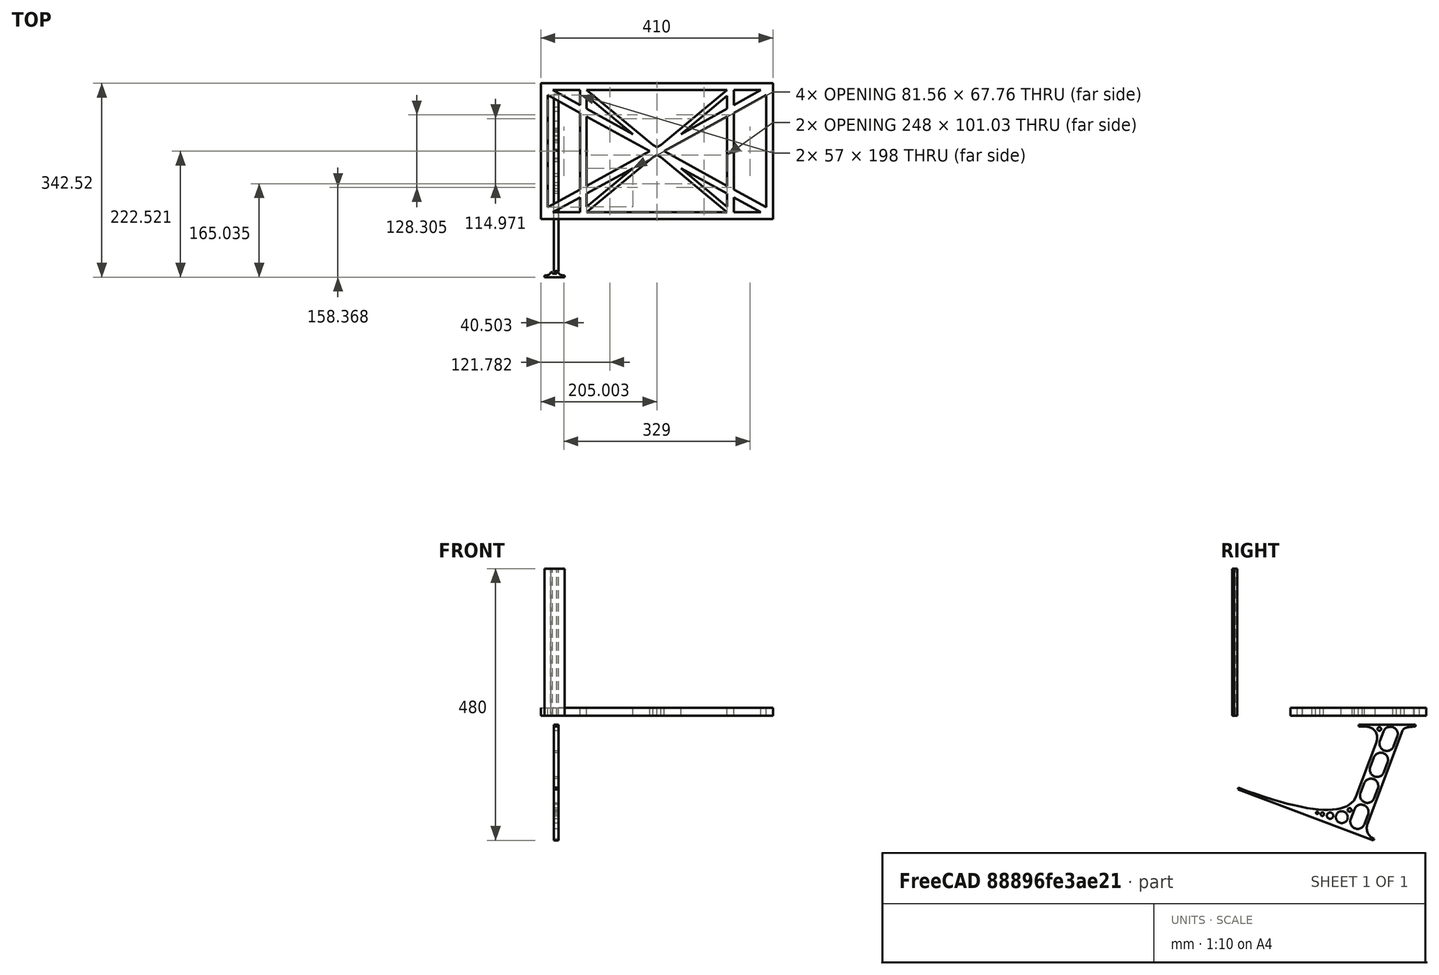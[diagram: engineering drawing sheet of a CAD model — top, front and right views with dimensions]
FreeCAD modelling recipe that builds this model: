
FCSTD DOCUMENT  (FreeCAD 0.19R0.19.2)
Label: laptopStand055
License: All rights reserved
LicenseURL: http://en.wikipedia.org/wiki/All_rights_reserved
objects: Sketcher::SketchObject×3, Part::Extrusion×3
note: 6 computed .brp shape members not serialized (recipe doc carries the construction recipe); baked Part::Feature solids carry a one-line shape summary decoded from their .brp

FEATURE [Sketcher::SketchObject] Sketch
  FullyConstrained = false
  sketch-geometry (94):
    g0: LineSegment StartX=-22.9272 StartY=136.221 StartZ=0 EndX=387.073 EndY=136.221 EndZ=0
    g1: LineSegment StartX=-22.9272 StartY=-103.779 StartZ=0 EndX=387.073 EndY=-103.779 EndZ=0
    g2: LineSegment StartX=375.073 StartY=115.221 StartZ=0 EndX=318.073 EndY=83.9235 EndZ=0
    g3: LineSegment StartX=-10.9272 StartY=-82.7794 StartZ=0 EndX=46.0728 EndY=-51.4823 EndZ=0
    g4: LineSegment StartX=-1.92718 StartY=124.221 StartZ=0 EndX=46.0728 EndY=97.8651 EndZ=0
    g5: LineSegment StartX=366.073 StartY=-91.7794 StartZ=0 EndX=318.073 EndY=-65.424 EndZ=0
    g6: LineSegment StartX=-10.9272 StartY=115.221 StartZ=0 EndX=-10.9272 EndY=-82.7794 EndZ=0
    g7: LineSegment StartX=375.073 StartY=-82.7794 StartZ=0 EndX=375.073 EndY=115.221 EndZ=0
    g8: LineSegment StartX=-1.92719 StartY=-91.7794 StartZ=0 EndX=46.0728 EndY=-91.7794 EndZ=0
    g9: LineSegment StartX=318.073 StartY=124.221 StartZ=0 EndX=366.073 EndY=124.221 EndZ=0
    g10: LineSegment StartX=306.073 StartY=-81.8102 StartZ=0 EndX=224.513 EndY=-14.0532 EndZ=0
    g11: LineSegment StartX=58.0728 StartY=114.251 StartZ=0 EndX=139.632 EndY=46.4944 EndZ=0
    g12: LineSegment StartX=306.073 StartY=124.221 StartZ=0 EndX=189.124 EndY=27.0628 EndZ=0
    g13: LineSegment StartX=58.0728 StartY=-91.7794 StartZ=0 EndX=175.022 EndY=5.37834 EndZ=0
    g14: LineSegment StartX=46.0728 StartY=124.221 StartZ=0 EndX=46.0728 EndY=97.8651 EndZ=0
    g15: LineSegment StartX=58.0728 StartY=-81.8102 StartZ=0 EndX=58.0728 EndY=-58.8351 EndZ=0
    g16: LineSegment StartX=318.073 StartY=124.221 StartZ=0 EndX=318.073 EndY=97.8651 EndZ=0
    g17: LineSegment StartX=306.073 StartY=114.251 StartZ=0 EndX=306.073 EndY=91.2763 EndZ=0
    g18: LineSegment StartX=224.513 StartY=46.4944 StartZ=0 EndX=306.073 EndY=114.251 EndZ=0
    g19: LineSegment StartX=175.022 StartY=27.0628 StartZ=0 EndX=58.0728 EndY=124.221 EndZ=0
    g20: LineSegment StartX=169.377 StartY=16.2206 StartZ=0 EndX=58.0728 EndY=77.3346 EndZ=0
    g21: LineSegment StartX=139.632 StartY=-14.0532 StartZ=0 EndX=58.0728 EndY=-81.8102 EndZ=0
    g22: LineSegment StartX=194.768 StartY=16.2206 StartZ=0 EndX=306.073 EndY=-44.8935 EndZ=0
    g23: LineSegment StartX=224.513 StartY=46.4944 StartZ=0 EndX=306.073 EndY=91.2763 EndZ=0
    g24: LineSegment StartX=139.632 StartY=-14.0532 StartZ=0 EndX=58.0728 EndY=-58.8351 EndZ=0
    g25: LineSegment StartX=189.124 StartY=5.37834 StartZ=0 EndX=306.073 EndY=-91.7794 EndZ=0
    g26: LineSegment StartX=306.073 StartY=77.3346 StartZ=0 EndX=306.073 EndY=-44.8935 EndZ=0
    g27: LineSegment StartX=318.073 StartY=83.9235 StartZ=0 EndX=318.073 EndY=-51.4823 EndZ=0
    g28: LineSegment StartX=318.073 StartY=97.8651 StartZ=0 EndX=366.073 EndY=124.221 EndZ=0
    g29: LineSegment StartX=306.073 StartY=77.3346 StartZ=0 EndX=194.768 EndY=16.2206 EndZ=0
    g30: LineSegment StartX=306.073 StartY=-58.8351 StartZ=0 EndX=224.513 EndY=-14.0532 EndZ=0
    g31: LineSegment StartX=306.073 StartY=-58.8351 StartZ=0 EndX=306.073 EndY=-81.8102 EndZ=0
    g32: LineSegment StartX=318.073 StartY=-51.4823 StartZ=0 EndX=375.073 EndY=-82.7794 EndZ=0
    g33: LineSegment StartX=318.073 StartY=-65.424 StartZ=0 EndX=318.073 EndY=-91.7794 EndZ=0
    g34: LineSegment StartX=318.073 StartY=-91.7794 StartZ=0 EndX=366.073 EndY=-91.7794 EndZ=0
    g35: LineSegment StartX=58.0728 StartY=-44.8935 StartZ=0 EndX=58.0728 EndY=77.3346 EndZ=0
    g36: LineSegment StartX=46.0728 StartY=-65.424 StartZ=0 EndX=-1.92719 EndY=-91.7794 EndZ=0
    g37: LineSegment StartX=46.0728 StartY=-65.424 StartZ=0 EndX=46.0728 EndY=-91.7794 EndZ=0
    g38: LineSegment StartX=58.0728 StartY=-44.8935 StartZ=0 EndX=169.377 EndY=16.2206 EndZ=0
    g39: LineSegment StartX=58.0728 StartY=91.2763 StartZ=0 EndX=58.0728 EndY=114.251 EndZ=0
    g40: LineSegment StartX=46.0728 StartY=83.9235 StartZ=0 EndX=46.0728 EndY=-51.4823 EndZ=0
    g41: LineSegment StartX=46.0728 StartY=124.221 StartZ=0 EndX=-1.92719 EndY=124.221 EndZ=0
    g42: LineSegment StartX=58.0728 StartY=91.2763 StartZ=0 EndX=139.632 EndY=46.4944 EndZ=0
    g43: LineSegment StartX=46.0728 StartY=83.9235 StartZ=0 EndX=-10.9272 EndY=115.221 EndZ=0
    g44: LineSegment StartX=-22.9272 StartY=136.221 StartZ=0 EndX=-42.9272 EndY=136.221 EndZ=0
    g45: LineSegment StartX=387.073 StartY=136.221 StartZ=0 EndX=407.073 EndY=136.221 EndZ=0
    g46: LineSegment StartX=-42.9272 StartY=136.221 StartZ=0 EndX=-42.9272 EndY=-103.779 EndZ=0
    g47: LineSegment StartX=-22.9272 StartY=-103.779 StartZ=0 EndX=-42.9272 EndY=-103.779 EndZ=0
    g48: LineSegment StartX=407.073 StartY=136.221 StartZ=0 EndX=407.073 EndY=-103.779 EndZ=0
    g49: LineSegment StartX=387.073 StartY=-103.779 StartZ=0 EndX=407.073 EndY=-103.779 EndZ=0
    g50: LineSegment StartX=179.022 StartY=27.0628 StartZ=0 EndX=179.022 EndY=124.221 EndZ=0
    g51: LineSegment StartX=185.124 StartY=27.0628 StartZ=0 EndX=185.124 EndY=124.221 EndZ=0
    g52: ArcOfCircle CenterX=-26.9272 CenterY=22.1087 CenterZ=0 NormalX=0 NormalY=0 NormalZ=1 AngleXU=0 Radius=8 StartAngle=1e-16 EndAngle=3.14159
    g53: ArcOfCircle CenterX=-26.9272 CenterY=-83.7794 CenterZ=0 NormalX=0 NormalY=0 NormalZ=1 AngleXU=0 Radius=8 StartAngle=3.14159 EndAngle=6.28319
    g54: LineSegment StartX=-34.9272 StartY=22.1087 StartZ=0 EndX=-34.9272 EndY=-83.7794 EndZ=0
    g55: LineSegment StartX=-18.9272 StartY=22.1087 StartZ=0 EndX=-18.9272 EndY=-83.7794 EndZ=0
    g56: LineSegment StartX=185.124 StartY=-91.7794 StartZ=0 EndX=306.073 EndY=-91.7794 EndZ=0
    g57: LineSegment StartX=179.022 StartY=-91.7794 StartZ=0 EndX=58.0728 EndY=-91.7794 EndZ=0
    g58: LineSegment StartX=306.073 StartY=124.221 StartZ=0 EndX=185.124 EndY=124.221 EndZ=0
    g59: LineSegment StartX=179.022 StartY=124.221 StartZ=0 EndX=58.0728 EndY=124.221 EndZ=0
    g60: ArcOfCircle CenterX=391.073 CenterY=22.1087 CenterZ=0 NormalX=0 NormalY=0 NormalZ=1 AngleXU=0 Radius=8 StartAngle=-4.4e-15 EndAngle=3.14159
    g61: LineSegment StartX=399.073 StartY=22.1087 StartZ=0 EndX=399.073 EndY=-83.7794 EndZ=0
    g62: LineSegment StartX=383.073 StartY=22.1087 StartZ=0 EndX=383.073 EndY=-83.7794 EndZ=0
    g63: ArcOfCircle CenterX=391.073 CenterY=-83.7794 CenterZ=0 NormalX=0 NormalY=0 NormalZ=1 AngleXU=0 Radius=8 StartAngle=3.14159 EndAngle=6.28319
    g64: Circle CenterX=175.022 CenterY=27.0628 CenterZ=0 NormalX=0 NormalY=0 NormalZ=1 AngleXU=0 Radius=1
    g65: Circle CenterX=179.022 CenterY=24.8665 CenterZ=0 NormalX=0 NormalY=0 NormalZ=1 AngleXU=0 Radius=1
    g66: Circle CenterX=179.022 CenterY=27.0628 CenterZ=0 NormalX=0 NormalY=0 NormalZ=1 AngleXU=0 Radius=1
    g67: BSplineCurve PolesCount=3 KnotsCount=2 Degree=2 IsPeriodic=0
    g68: GeomPoint X=175.022 Y=27.0628 Z=0
    g69: GeomPoint X=179.022 Y=27.0628 Z=0
    g70: Circle CenterX=189.124 CenterY=27.0628 CenterZ=0 NormalX=0 NormalY=0 NormalZ=1 AngleXU=0 Radius=1
    g71: Circle CenterX=185.124 CenterY=24.8665 CenterZ=0 NormalX=0 NormalY=0 NormalZ=1 AngleXU=0 Radius=1
    g72: Circle CenterX=185.124 CenterY=27.0628 CenterZ=0 NormalX=0 NormalY=0 NormalZ=1 AngleXU=0 Radius=1
    g73: BSplineCurve PolesCount=3 KnotsCount=2 Degree=2 IsPeriodic=0
    g74: GeomPoint X=189.124 Y=27.0628 Z=0
    g75: GeomPoint X=185.124 Y=27.0628 Z=0
    g76: Circle CenterX=175.022 CenterY=5.37834 CenterZ=0 NormalX=0 NormalY=0 NormalZ=1 AngleXU=0 Radius=1
    g77: Circle CenterX=179.022 CenterY=7.57463 CenterZ=0 NormalX=0 NormalY=0 NormalZ=1 AngleXU=0 Radius=1
    g78: Circle CenterX=179.022 CenterY=5.34704 CenterZ=0 NormalX=0 NormalY=0 NormalZ=1 AngleXU=0 Radius=1
    g79: BSplineCurve PolesCount=3 KnotsCount=2 Degree=2 IsPeriodic=0
    g80: GeomPoint X=175.022 Y=5.37834 Z=0
    g81: GeomPoint X=179.022 Y=5.34704 Z=0
    g82: Circle CenterX=189.124 CenterY=5.37834 CenterZ=0 NormalX=0 NormalY=0 NormalZ=1 AngleXU=0 Radius=1
    g83: Circle CenterX=185.124 CenterY=7.57463 CenterZ=0 NormalX=0 NormalY=0 NormalZ=1 AngleXU=0 Radius=1
    g84: Circle CenterX=185.124 CenterY=5.34704 CenterZ=0 NormalX=0 NormalY=0 NormalZ=1 AngleXU=0 Radius=1
    g85: BSplineCurve PolesCount=3 KnotsCount=2 Degree=2 IsPeriodic=0
    g86: GeomPoint X=189.124 Y=5.37834 Z=0
    g87: GeomPoint X=185.124 Y=5.34704 Z=0
    g88: LineSegment StartX=179.022 StartY=5.34704 StartZ=0 EndX=179.022 EndY=-91.7794 EndZ=0
    g89: LineSegment StartX=185.124 StartY=-91.7794 StartZ=0 EndX=185.124 EndY=5.34704 EndZ=0
    g90: LineSegment StartX=169.377 StartY=16.2206 StartZ=0 EndX=165.871 EndY=14.2954 EndZ=0
    g91: LineSegment StartX=195.975 StartY=19.7951 StartZ=0 EndX=192.508 EndY=17.8011 EndZ=0
    g92: LineSegment StartX=169.377 StartY=16.2206 StartZ=0 EndX=165.871 EndY=18.1458 EndZ=0
    g93: LineSegment StartX=198.275 StartY=14.2954 StartZ=0 EndX=194.768 EndY=16.2206 EndZ=0
  constraints (186):
    c: Horizontal(g0)
    c: Distance(g0) = 410
    c: Horizontal(g1)
    c: Block(g0)
    c: Horizontal(g8)
    c: Horizontal(g9)
    c: Tangent(g5,g20)
    c: PointOnObject(g20,g3)
    c: PointOnObject(g22,g2)
    c: Coincident(g42,g11)
    c: Coincident(g18,g23)
    c: Coincident(g24,g21)
    c: Coincident(g30,g10)
    c: Coincident(g18,g17)
    c: Tangent(g17,g26)
    c: Tangent(g16,g27)
    c: Coincident(g23,g17)
    c: Tangent(g23,g28)
    c: Coincident(g2,g27)
    c: Coincident(g29,g26)
    c: Tangent(g2,g29)
    c: Coincident(g31,g10)
    c: Tangent(g5,g30)
    c: Tangent(g26,g31)
    c: Coincident(g22,g26)
    c: Tangent(g22,g32)
    c: Coincident(g27,g32)
    c: Coincident(g33,g5)
    c: Tangent(g27,g33)
    c: Coincident(g21,g15)
    c: Tangent(g15,g35)
    c: Coincident(g24,g15)
    c: Tangent(g24,g36)
    c: Coincident(g37,g36)
    c: Tangent(g14,g37)
    c: Coincident(g3,g40)
    c: Coincident(g38,g35)
    c: Tangent(g35,g39)
    c: Tangent(g14,g40)
    c: Coincident(g11,g39)
    c: Coincident(g4,g14)
    c: Coincident(g42,g39)
    c: Tangent(g4,g42)
    c: Coincident(g20,g35)
    c: Coincident(g43,g40)
    c: Tangent(g20,g43)
    c: Block(g19)
    c: Block(g12)
    c: Block(g16)
    c: Block(g28)
    c: Block(g2)
    c: Block(g32)
    c: Block(g7)
    c: Block(g30)
    c: Block(g31)
    c: Block(g5)
    c: Block(g33)
    c: Block(g18)
    c: Block(g25)
    c: Block(g13)
    c: Block(g24)
    c: Block(g21)
    c: Block(g37)
    c: Block(g36)
    c: Block(g3)
    c: Block(g6)
    c: Block(g43)
    c: Block(g4)
    c: Block(g14)
    c: Block(g11)
    c: Block(g39)
    c: Block(g29)
    c: Block(g26)
    c: Block(g20)
    c: Block(g38)
    c: Block(g41)
    c: Block(g9)
    c: Block(g34)
    c: Block(g8)
    c: Horizontal(g44)
    c: Distance(g44) = 20
    c: Coincident(g45,g0)
    c: Horizontal(g45)
    c: Distance(g45) = 20
    c: Coincident(g46,g44)
    c: Vertical(g46)
    c: Horizontal(g47)
    c: Coincident(g47,g46)
    c: Coincident(g48,g45)
    c: Vertical(g48)
    c: Coincident(g49,g1)
    c: Horizontal(g49)
    c: Coincident(g49,g48)
    c: Block(g48)
    c: Block(g47)
    c: Block(g46)
    c: Block(g1)
    c: Vertical(g50)
    c: Vertical(g51)
    c: Block(g50)
    c: Block(g51)
    c: Tangent(g52,g55) = 1.5708
    c: Tangent(g52,g54) = -1.5708
    c: Tangent(g54,g53) = -1.5708
    c: Tangent(g55,g53) = 1.5708
    c: Vertical(g54)
    c: Equal(g52,g53)
    c: Block(g55)
    c: Block(g54)
    c: Coincident(g56,g25)
    c: Horizontal(g56)
    c: Coincident(g57,g13)
    c: Horizontal(g57)
    c: Coincident(g58,g12)
    c: Coincident(g58,g51)
    c: Horizontal(g58)
    c: Coincident(g59,g50)
    c: Coincident(g59,g19)
    c: Horizontal(g59)
    c: Distance(g49) = 20
    c: Distance(g1) = 410
    c: Tangent(g60,g61) = 1.5708
    c: Tangent(g61,g63) = 1.5708
    c: Equal(g60,g63)
    c: Coincident(g62,g60)
    c: Coincident(g62,g63)
    c: Block(g61)
    c: Block(g62)
    c: Block(g22)
    c: Coincident(g67,g19)
    c: Weight(g64) = 1
    c: Equal(g64,g65)
    c: Equal(g64,g66)
    c: Coincident(g67,g50)
    c: InternalAlignment(g64,g67)
    c: InternalAlignment(g65,g67)
    c: InternalAlignment(g66,g67)
    c: InternalAlignment(g68,g67)
    c: InternalAlignment(g69,g67)
    c: Coincident(g73,g12)
    c: Weight(g70) = 1
    c: Equal(g70,g71)
    c: Equal(g70,g72)
    c: Coincident(g73,g51)
    c: InternalAlignment(g70,g73)
    c: InternalAlignment(g71,g73)
    c: InternalAlignment(g72,g73)
    c: InternalAlignment(g74,g73)
    c: InternalAlignment(g75,g73)
    c: Block(g73)
    c: Block(g67)
    c: Coincident(g79,g13)
    c: Weight(g76) = 1
    c: Equal(g76,g77)
    c: Equal(g76,g78)
    c: InternalAlignment(g76,g79)
    c: InternalAlignment(g77,g79)
    c: InternalAlignment(g78,g79)
    c: InternalAlignment(g80,g79)
    c: InternalAlignment(g81,g79)
    c: Weight(g82) = 1
    c: Equal(g82,g83)
    c: Equal(g82,g84)
    c: InternalAlignment(g82,g85)
    c: InternalAlignment(g83,g85)
    c: InternalAlignment(g84,g85)
    c: InternalAlignment(g86,g85)
    c: InternalAlignment(g87,g85)
    c: Block(g85)
    c: Block(g79)
    c: Coincident(g88,g79)
    c: Coincident(g88,g57)
    c: Vertical(g88)
    c: Coincident(g89,g56)
    c: Coincident(g89,g85)
    c: Vertical(g89)
    c: Distance(g90) = 4
    c: Parallel(g38,g90)
    c: Equal(g90,g91) = 4
    c: Distance(g92) = 4
    c: Equal(g92,g93) = 4
    c: Coincident(g90,g20)
    c: Coincident(g92,g20)
    c: Parallel(g92,g20)
    c: Coincident(g93,g22)
    c: Parallel(g22,g93)
FEATURE [Sketcher::SketchObject] Sketch001
  FullyConstrained = true
  MapMode = 4
  Placement = pos=(0,0,0) rot=(0.57735,0.57735,0.57735;2.0944rad)
  Support = -> [Sketch]
  sketch-geometry (46):
    g0: BSplineCurve PolesCount=3 KnotsCount=2 Degree=2 IsPeriodic=0
    g1: ArcOfCircle CenterX=73.122 CenterY=-32.2909 CenterZ=0 NormalX=0 NormalY=0 NormalZ=1 AngleXU=0 Radius=13 StartAngle=5.92268 EndAngle=9.06428
    g2: ArcOfCircle CenterX=66.7816 CenterY=-49.1439 CenterZ=0 NormalX=0 NormalY=0 NormalZ=1 AngleXU=0 Radius=13 StartAngle=2.78068 EndAngle=5.92131
    g3: ArcOfCircle CenterX=55.9263 CenterY=-78.1807 CenterZ=0 NormalX=0 NormalY=0 NormalZ=1 AngleXU=0 Radius=13 StartAngle=5.92268 EndAngle=9.06428
    g4: ArcOfCircle CenterX=49.5884 CenterY=-95.0342 CenterZ=0 NormalX=0 NormalY=0 NormalZ=1 AngleXU=0 Radius=13 StartAngle=2.78068 EndAngle=5.92131
    g5: ArcOfCircle CenterX=38.7206 CenterY=-124.067 CenterZ=0 NormalX=0 NormalY=0 NormalZ=1 AngleXU=0 Radius=13 StartAngle=5.92268 EndAngle=9.06428
    g6: ArcOfCircle CenterX=32.3875 CenterY=-140.92 CenterZ=0 NormalX=0 NormalY=0 NormalZ=1 AngleXU=0 Radius=13 StartAngle=2.78068 EndAngle=5.92131
    g7: ArcOfCircle CenterX=21.4715 CenterY=-169.934 CenterZ=0 NormalX=0 NormalY=0 NormalZ=1 AngleXU=0 Radius=13 StartAngle=5.92268 EndAngle=9.06428
    g8: ArcOfCircle CenterX=15.1336 CenterY=-186.787 CenterZ=0 NormalX=0 NormalY=0 NormalZ=1 AngleXU=0 Radius=13 StartAngle=2.78068 EndAngle=5.92131
    g9-g12: Circle x4 (B-spline internal-alignment scaffolding for g13; pole/knot coordinates omitted)
    g13: BSplineCurve PolesCount=4 KnotsCount=2 Degree=3 IsPeriodic=0
    g14: GeomPoint X=28.8094 Y=-19.0875 Z=0
    g15: GeomPoint X=47.0443 Y=-50.4712 Z=0
    g16: Circle CenterX=53.5586 CenterY=-23.2695 CenterZ=0 NormalX=0 NormalY=0 NormalZ=1 AngleXU=0 Radius=3.24518
    g17: Circle CenterX=-195.441 CenterY=-127.082 CenterZ=0 NormalX=0 NormalY=0 NormalZ=1 AngleXU=0 Radius=1
    g18: Circle CenterX=-8.24091 CenterY=-197.481 CenterZ=0 NormalX=0 NormalY=0 NormalZ=1 AngleXU=0 Radius=1
    g19: Circle CenterX=12.8789 CenterY=-141.321 CenterZ=0 NormalX=0 NormalY=0 NormalZ=1 AngleXU=0 Radius=1
    g20: BSplineCurve PolesCount=3 KnotsCount=2 Degree=2 IsPeriodic=0
    g21: GeomPoint X=-195.441 Y=-127.082 Z=0
    g22: GeomPoint X=12.8789 Y=-141.321 Z=0
    g23: Circle CenterX=-12.8016 CenterY=-179.036 CenterZ=0 NormalX=0 NormalY=0 NormalZ=1 AngleXU=0 Radius=10.5072
    g24: Circle CenterX=0.933922 CenterY=-166.43 CenterZ=0 NormalX=0 NormalY=0 NormalZ=1 AngleXU=0 Radius=3.26661
    g25: Circle CenterX=-33.5518 CenterY=-176.44 CenterZ=0 NormalX=0 NormalY=0 NormalZ=1 AngleXU=0 Radius=5.64388
    g26: Circle CenterX=-47.2366 CenterY=-173.859 CenterZ=0 NormalX=0 NormalY=0 NormalZ=1 AngleXU=0 Radius=3.01653
    g27: Circle CenterX=-56.2595 CenterY=-171.456 CenterZ=0 NormalX=0 NormalY=0 NormalZ=1 AngleXU=0 Radius=2.12826
    g28: ArcOfCircle CenterX=51.2151 CenterY=-198.473 CenterZ=0 NormalX=0 NormalY=0 NormalZ=1 AngleXU=0 Radius=20 StartAngle=2.78189 EndAngle=4.35269
    g29: LineSegment StartX=32.4951 StartY=-191.433 StartZ=0 EndX=94.6577 EndY=-26.1351 EndZ=0
    g30: LineSegment StartX=43.1192 StartY=-220.001 StartZ=0 EndX=-196.497 EndY=-129.89 EndZ=0
    g31: LineSegment StartX=43.1192 StartY=-220.001 StartZ=0 EndX=44.1752 EndY=-217.193 EndZ=0
    g32: LineSegment StartX=117.223 StartY=-19.0875 StartZ=0 EndX=117.223 EndY=-16.0875 EndZ=0
    g33: LineSegment StartX=117.223 StartY=-16.0875 StartZ=0 EndX=17.2232 EndY=-16.0875 EndZ=0
    g34: LineSegment StartX=17.2232 StartY=-16.0875 StartZ=0 EndX=17.2232 EndY=-19.0875 EndZ=0
    g35: LineSegment StartX=28.8094 StartY=-19.0875 StartZ=0 EndX=17.2232 EndY=-19.0875 EndZ=0
    g36: LineSegment StartX=47.0443 StartY=-50.4712 StartZ=0 EndX=12.8789 EndY=-141.321 EndZ=0
    g37: LineSegment StartX=-195.441 StartY=-127.082 StartZ=0 EndX=-196.497 EndY=-129.89 EndZ=0
    g38: LineSegment StartX=85.2864 StartY=-36.8765 StartZ=0 EndX=78.9396 EndY=-53.7463 EndZ=0
    g39: LineSegment StartX=60.9577 StartY=-27.7052 StartZ=0 EndX=54.6191 EndY=-44.5532 EndZ=0
    g40: LineSegment StartX=68.0907 StartY=-82.7664 StartZ=0 EndX=61.7465 EndY=-99.6365 EndZ=0
    g41: LineSegment StartX=43.7619 StartY=-73.595 StartZ=0 EndX=37.426 EndY=-90.4435 EndZ=0
    g42: LineSegment StartX=50.885 StartY=-128.652 StartZ=0 EndX=44.5456 EndY=-145.522 EndZ=0
    g43: LineSegment StartX=26.5562 StartY=-119.481 StartZ=0 EndX=20.2251 EndY=-136.329 EndZ=0
    g44: LineSegment StartX=9.3071 StartY=-165.349 StartZ=0 EndX=2.97115 EndY=-182.197 EndZ=0
    g45: LineSegment StartX=33.6358 StartY=-174.52 StartZ=0 EndX=27.2917 EndY=-191.39 EndZ=0
  constraints (70):
    c: Block(g0)
    c: Block(g1)
    c: Block(g2)
    c: Block(g4)
    c: Block(g3)
    c: Block(g6)
    c: Block(g5)
    c: Block(g8)
    c: Block(g7)
    c: Weight(g9) = 1
    c: Equal(g9,g10)
    c: Equal(g9,g11)
    c: Equal(g9,g12)
    c: InternalAlignment(g9-g12 -> g13) x4
    c: InternalAlignment(g14,g13)
    c: InternalAlignment(g15,g13)
    c: Block(g16)
    c: Weight(g17) = 1
    c: Equal(g17,g18)
    c: Equal(g17,g19)
    c: InternalAlignment(g17,g20)
    c: InternalAlignment(g18,g20)
    c: InternalAlignment(g19,g20)
    c: InternalAlignment(g21,g20)
    c: InternalAlignment(g22,g20)
    c: Block(g20)
    c: Block(g23)
    c: Block(g24)
    c: Block(g25)
    c: Block(g26)
    c: Block(g27)
    c: Block(g28)
    c: Coincident(g29,g28)
    c: Coincident(g29,g0)
    c: Block(g13)
    c: Coincident(g31,g30)
    c: Coincident(g31,g28)
    c: Block(g31)
    c: Coincident(g32,g0)
    c: Vertical(g32)
    c: Coincident(g33,g32)
    c: Horizontal(g33)
    c: Coincident(g34,g33)
    c: Vertical(g34)
    c: Block(g33)
    c: Coincident(g35,g13)
    c: Coincident(g35,g34)
    c: Horizontal(g35)
    c: Coincident(g36,g13)
    c: Coincident(g36,g20)
    c: Coincident(g37,g20)
    c: Coincident(g37,g30)
    c: Block(g30)
    c: Coincident(g38,g1)
    c: Coincident(g38,g2)
    c: Coincident(g39,g1)
    c: Coincident(g39,g2)
    c: Coincident(g40,g3)
    c: Coincident(g40,g4)
    c: Coincident(g41,g3)
    c: Coincident(g41,g4)
    c: Coincident(g42,g5)
    c: Coincident(g42,g6)
    c: Coincident(g43,g5)
    c: Coincident(g43,g6)
    c: Coincident(g44,g7)
    c: Coincident(g44,g8)
    c: Coincident(g45,g7)
    c: Coincident(g45,g8)
    c: Distance(g30) = 256
FEATURE [Part::Extrusion] Extrude002
  Base = -> Sketch001
  Dir = (1,0,0)
  DirMode = 2
  FaceMakerClass = Part::FaceMakerBullseye
  LengthFwd = 8
  LengthRev = 0
  Solid = true
  Symmetric = false
FEATURE [Sketcher::SketchObject] Sketch002
  FullyConstrained = true
  sketch-geometry (20):
    g0: LineSegment StartX=-2.77179 StartY=-200.304 StartZ=0 EndX=5.22821 EndY=-200.304 EndZ=0
    g1: LineSegment StartX=5.22821 StartY=-200.304 StartZ=0 EndX=5.22821 EndY=-197.304 EndZ=0
    g2: LineSegment StartX=-2.77179 StartY=-200.304 StartZ=0 EndX=-2.77179 EndY=-197.304 EndZ=0
    g3: LineSegment StartX=5.22821 StartY=-197.304 StartZ=0 EndX=8.22821 EndY=-197.304 EndZ=0
    g4: LineSegment StartX=-2.77179 StartY=-197.304 StartZ=0 EndX=-5.77179 EndY=-197.304 EndZ=0
    g5: LineSegment StartX=19.2282 StartY=-203.304 StartZ=0 EndX=19.2282 EndY=-206.304 EndZ=0
    g6: LineSegment StartX=-16.7718 StartY=-203.304 StartZ=0 EndX=-16.7718 EndY=-206.304 EndZ=0
    g7: LineSegment StartX=-16.7718 StartY=-206.304 StartZ=0 EndX=19.2282 EndY=-206.304 EndZ=0
    g8: Circle CenterX=-16.7718 CenterY=-203.304 CenterZ=0 NormalX=0 NormalY=0 NormalZ=1 AngleXU=0 Radius=1
    g9: Circle CenterX=-5.77179 CenterY=-203.304 CenterZ=0 NormalX=0 NormalY=0 NormalZ=1 AngleXU=0 Radius=1
    g10: Circle CenterX=-5.77179 CenterY=-197.304 CenterZ=0 NormalX=0 NormalY=0 NormalZ=1 AngleXU=0 Radius=1
    g11: BSplineCurve PolesCount=3 KnotsCount=2 Degree=2 IsPeriodic=0
    g12: GeomPoint X=-16.7718 Y=-203.304 Z=0
    g13: GeomPoint X=-5.77179 Y=-197.304 Z=0
    g14: Circle CenterX=19.2282 CenterY=-203.304 CenterZ=0 NormalX=0 NormalY=0 NormalZ=1 AngleXU=0 Radius=1
    g15: Circle CenterX=8.22821 CenterY=-203.304 CenterZ=0 NormalX=0 NormalY=0 NormalZ=1 AngleXU=0 Radius=1
    g16: Circle CenterX=8.22821 CenterY=-197.304 CenterZ=0 NormalX=0 NormalY=0 NormalZ=1 AngleXU=0 Radius=1
    g17: BSplineCurve PolesCount=3 KnotsCount=2 Degree=2 IsPeriodic=0
    g18: GeomPoint X=19.2282 Y=-203.304 Z=0
    g19: GeomPoint X=8.22821 Y=-197.304 Z=0
  constraints (41):
    c: Horizontal(g0)
    c: Distance(g0) = 8
    c: Coincident(g1,g0)
    c: Vertical(g1)
    c: Distance(g1) = 3
    c: Coincident(g2,g0)
    c: Vertical(g2)
    c: Distance(g2) = 3
    c: Coincident(g3,g1)
    c: Horizontal(g3)
    c: Distance(g3) = 3
    c: Coincident(g4,g2)
    c: Horizontal(g4)
    c: Distance(g4) = 3
    c: Vertical(g5)
    c: Vertical(g6)
    c: Coincident(g7,g6)
    c: Coincident(g7,g5)
    c: Weight(g8) = 1
    c: Equal(g8,g9)
    c: Equal(g8,g10)
    c: Coincident(g11,g4)
    c: InternalAlignment(g8,g11)
    c: InternalAlignment(g9,g11)
    c: InternalAlignment(g10,g11)
    c: InternalAlignment(g12,g11)
    c: InternalAlignment(g13,g11)
    c: Coincident(g17,g5)
    c: Weight(g14) = 1
    c: Equal(g14,g15)
    c: Equal(g14,g16)
    c: Coincident(g17,g3)
    c: InternalAlignment(g14,g17)
    c: InternalAlignment(g15,g17)
    c: InternalAlignment(g16,g17)
    c: InternalAlignment(g18,g17)
    c: InternalAlignment(g19,g17)
    c: Block(g7)
    c: Block(g17)
    c: Block(g11)
    c: Block(g6)
FEATURE [Part::Extrusion] Extrude003
  Base = -> Sketch002
  Dir = (0,0,1)
  DirMode = 2
  FaceMakerClass = Part::FaceMakerBullseye
  LengthFwd = 260
  LengthRev = 0
  Solid = true
  Symmetric = false
FEATURE [Part::Extrusion] Extrude
  Base = -> Sketch
  Dir = (0,0,1)
  DirMode = 2
  FaceMakerClass = Part::FaceMakerBullseye
  LengthFwd = 14
  LengthRev = 0
  Solid = true
  Symmetric = false
